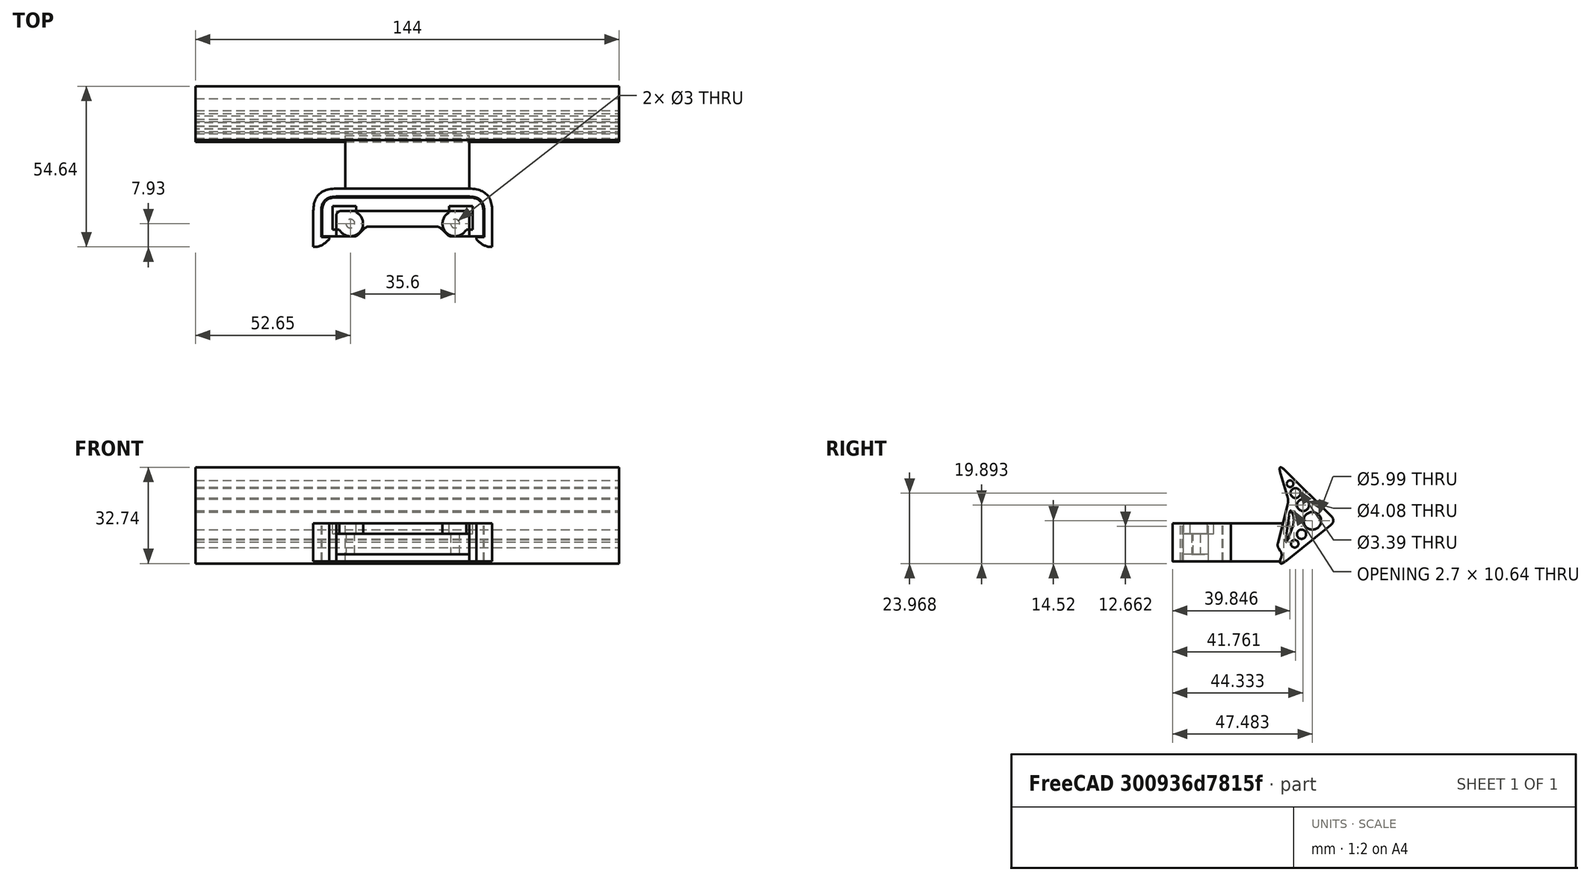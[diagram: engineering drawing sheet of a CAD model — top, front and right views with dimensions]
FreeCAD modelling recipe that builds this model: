
FCSTD DOCUMENT  (FreeCAD 0.19R0.19.2)
Label: 026
License: All rights reserved
LicenseURL: http://en.wikipedia.org/wiki/All_rights_reserved
objects: Sketcher::SketchObject×5, Part::Extrusion×5, Part::Box×1
note: 11 computed .brp shape members not serialized (recipe doc carries the construction recipe); baked Part::Feature solids carry a one-line shape summary decoded from their .brp

FEATURE [Sketcher::SketchObject] Sketch  label="attatchmentPiece"
  FullyConstrained = true
  sketch-geometry (20):
    g0: Circle CenterX=16.25 CenterY=0 CenterZ=0 NormalX=0 NormalY=0 NormalZ=1 AngleXU=0 Radius=1.5
    g1: LineSegment StartX=21.05 StartY=0 StartZ=0 EndX=21.05 EndY=-1 EndZ=0
    g2: LineSegment StartX=21.05 StartY=-1 StartZ=0 EndX=21.05 EndY=-4.3 EndZ=0
    g3: LineSegment StartX=-24.15 StartY=4.3 StartZ=0 EndX=21.05 EndY=4.3 EndZ=0
    g4: LineSegment StartX=21.05 StartY=0 StartZ=0 EndX=21.05 EndY=4.3 EndZ=0
    g5-g8: Circle x4 (B-spline internal-alignment scaffolding for g9; pole/knot coordinates omitted)
    g9: BSplineCurve PolesCount=4 KnotsCount=2 Degree=3 IsPeriodic=0
    g10: GeomPoint X=10.05 Y=-1 Z=0
    g11: GeomPoint X=14.55 Y=-4.3 Z=0
    g12: LineSegment StartX=10.05 StartY=-1 StartZ=0 EndX=-10.05 EndY=-1 EndZ=0
    g13: LineSegment StartX=14.55 StartY=-4.3 StartZ=0 EndX=21.05 EndY=-4.3 EndZ=0
    g14: LineSegment StartX=-24.15 StartY=4.3 StartZ=0 EndX=-24.15 EndY=-4.3 EndZ=0
    g15: LineSegment StartX=-13.15 StartY=-1 StartZ=0 EndX=-10.05 EndY=-1 EndZ=0
    g16: LineSegment StartX=-24.15 StartY=-4.3 StartZ=0 EndX=-19.35 EndY=-4.3 EndZ=0
    g17: Circle CenterX=-19.35 CenterY=0 CenterZ=0 NormalX=0 NormalY=0 NormalZ=1 AngleXU=0 Radius=1.5
    g18: LineSegment StartX=-19.35 StartY=-4.3 StartZ=0 EndX=-17.65 EndY=-4.3 EndZ=0
    g19: BSplineCurve PolesCount=4 KnotsCount=2 Degree=3 IsPeriodic=0
  constraints (41):
    c: Block(g0)
    c: Vertical(g1)
    c: Coincident(g2,g1)
    c: Vertical(g2)
    c: Block(g1)
    c: Horizontal(g3)
    c: Vertical(g4)
    c: Coincident(g4,g3)
    c: Block(g3)
    c: Block(g4)
    c: Weight(g5) = 1
    c: Equal(g5,g6)
    c: Equal(g5,g7)
    c: Equal(g5,g8)
    c: InternalAlignment(g5-g8 -> g9) x4
    c: InternalAlignment(g10,g9)
    c: InternalAlignment(g11,g9)
    c: Block(g9)
    c: Coincident(g12,g9)
    c: Horizontal(g12)
    c: Coincident(g13,g9)
    c: Coincident(g13,g2)
    c: Horizontal(g13)
    c: Distance(g3) = 45.2
    c: Coincident(g14,g3)
    c: Vertical(g14)
    c: Horizontal(g15)
    c: Distance(g15) = 3.1
    c: Block(g17)
    c: Horizontal(g16)
    c: Block(g19)
    c: Coincident(g18,g16)
    c: Coincident(g18,g19)
    c: Horizontal(g18)
    c: Block(g18)
    c: Coincident(g19,g15)
    c: Block(g16)
    c: Block(g12)
    c: Block(g14)
    c: Distance(g16) = 4.8
    c: Distance(g18) = 1.7
FEATURE [Part::Extrusion] Extrude  label="attatchmentPiece001"
  Base = -> Sketch
  Dir = (0,0,1)
  DirMode = 2
  FaceMakerClass = Part::FaceMakerBullseye
  LengthFwd = 7
  LengthRev = 0
  Solid = true
  Symmetric = false
FEATURE [Sketcher::SketchObject] Sketch001  label="attatchmentPieceSurround"
  FullyConstrained = true
  sketch-geometry (19):
    g0: LineSegment StartX=25.85 StartY=-4.3 StartZ=0 EndX=21.05 EndY=-4.3 EndZ=0
    g1: LineSegment StartX=25.85 StartY=-4.3 StartZ=0 EndX=25.85 EndY=4.3 EndZ=0
    g2: LineSegment StartX=-21.05 StartY=8.9 StartZ=0 EndX=21.05 EndY=8.9 EndZ=0
    g3: Circle CenterX=21.05 CenterY=8.9 CenterZ=0 NormalX=0 NormalY=0 NormalZ=1 AngleXU=0 Radius=1
    g4: Circle CenterX=25.85 CenterY=8.9 CenterZ=0 NormalX=0 NormalY=0 NormalZ=1 AngleXU=0 Radius=1
    g5: Circle CenterX=25.85 CenterY=4.3 CenterZ=0 NormalX=0 NormalY=0 NormalZ=1 AngleXU=0 Radius=1
    g6: BSplineCurve PolesCount=3 KnotsCount=2 Degree=2 IsPeriodic=0
    g7: GeomPoint X=21.05 Y=8.9 Z=0
    g8: GeomPoint X=25.85 Y=4.3 Z=0
    g9: ArcOfCircle CenterX=19.45 CenterY=2.7 CenterZ=0 NormalX=0 NormalY=0 NormalZ=1 AngleXU=0 Radius=1.6 StartAngle=0 EndAngle=1.5708
    g10: LineSegment StartX=-19.45 StartY=4.3 StartZ=0 EndX=19.45 EndY=4.3 EndZ=0
    g11: LineSegment StartX=21.05 StartY=2.7 StartZ=0 EndX=21.05 EndY=-4.3 EndZ=0
    g12: BSplineCurve PolesCount=3 KnotsCount=2 Degree=2 IsPeriodic=0
    g13: LineSegment StartX=-28.95 StartY=-4.3 StartZ=0 EndX=-28.95 EndY=4.3 EndZ=0
    g14: LineSegment StartX=-24.15 StartY=-4.3 StartZ=0 EndX=-28.95 EndY=-4.3 EndZ=0
    g15: LineSegment StartX=-24.15 StartY=2.7 StartZ=0 EndX=-24.15 EndY=-4.3 EndZ=0
    g16: ArcOfCircle CenterX=-22.55 CenterY=2.7 CenterZ=0 NormalX=0 NormalY=0 NormalZ=1 AngleXU=0 Radius=1.6 StartAngle=1.5708 EndAngle=3.14159
    g17: LineSegment StartX=-22.55 StartY=4.3 StartZ=0 EndX=-19.45 EndY=4.3 EndZ=0
    g18: LineSegment StartX=-24.15 StartY=8.9 StartZ=0 EndX=-21.05 EndY=8.9 EndZ=0
  constraints (41):
    c: Horizontal(g0)
    c: Vertical(g1)
    c: Coincident(g1,g0)
    c: Horizontal(g2)
    c: Distance(g2) = 42.1
    c: Block(g2)
    c: Coincident(g6,g2)
    c: Weight(g3) = 1
    c: Equal(g3,g4)
    c: Equal(g3,g5)
    c: Coincident(g6,g1)
    c: InternalAlignment(g3,g6)
    c: InternalAlignment(g4,g6)
    c: InternalAlignment(g5,g6)
    c: InternalAlignment(g7,g6)
    c: InternalAlignment(g8,g6)
    c: Block(g0)
    c: Block(g6)
    c: Block(g9)
    c: Coincident(g10,g9)
    c: Horizontal(g10)
    c: Coincident(g11,g9)
    c: Coincident(g11,g0)
    c: Vertical(g11)
    c: Horizontal(g14)
    c: Coincident(g13,g14)
    c: Vertical(g13)
    c: Coincident(g12,g13)
    c: Block(g13)
    c: Block(g12)
    c: Block(g16)
    c: Coincident(g15,g16)
    c: Coincident(g15,g14)
    c: Vertical(g15)
    c: Block(g10)
    c: Coincident(g17,g16)
    c: Coincident(g17,g10)
    c: Horizontal(g17)
    c: Coincident(g18,g12)
    c: Coincident(g18,g2)
    c: Horizontal(g18)
FEATURE [Part::Extrusion] Extrude001  label="attatchmentPieceSurround001"
  Base = -> Sketch001
  Dir = (0,0,1)
  DirMode = 2
  FaceMakerClass = Part::FaceMakerBullseye
  LengthFwd = 13
  LengthRev = 0
  Placement = pos=(0,0,-2.4) rot=(0,0,1;0rad)
  Solid = true
  Symmetric = false
FEATURE [Sketcher::SketchObject] Sketch002  label="attatchmentPieceEndScrewHoleCaps"
  FullyConstrained = true
  sketch-geometry (10):
    g0: ArcOfCircle CenterX=16.25 CenterY=0 CenterZ=0 NormalX=0 NormalY=0 NormalZ=1 AngleXU=0 Radius=4.3 StartAngle=2.05456 EndAngle=5.79942
    g1: LineSegment StartX=14.25 StartY=3.80657 StartZ=0 EndX=14.25 EndY=6 EndZ=0
    g2: LineSegment StartX=20.0566 StartY=-2 StartZ=0 EndX=22.25 EndY=-2 EndZ=0
    g3: LineSegment StartX=22.25 StartY=-2 StartZ=0 EndX=22.25 EndY=6 EndZ=0
    g4: LineSegment StartX=14.25 StartY=6 StartZ=0 EndX=22.25 EndY=6 EndZ=0
    g5: LineSegment StartX=-25.35 StartY=-2 StartZ=0 EndX=-25.35 EndY=6 EndZ=0
    g6: LineSegment StartX=-25.35 StartY=-2 StartZ=0 EndX=-23.1566 EndY=-2 EndZ=0
    g7: LineSegment StartX=-17.35 StartY=6 StartZ=0 EndX=-25.35 EndY=6 EndZ=0
    g8: LineSegment StartX=-17.35 StartY=3.80657 StartZ=0 EndX=-17.35 EndY=6 EndZ=0
    g9: ArcOfCircle CenterX=-19.35 CenterY=0 CenterZ=0 NormalX=0 NormalY=0 NormalZ=1 AngleXU=0 Radius=4.3 StartAngle=3.62536 EndAngle=7.37022
  constraints (25):
    c: Block(g0)
    c: Vertical(g1)
    c: Horizontal(g2)
    c: Coincident(g3,g2)
    c: Vertical(g3)
    c: Coincident(g4,g1)
    c: Horizontal(g4)
    c: Coincident(g3,g4)
    c: Block(g4)
    c: Block(g3)
    c: Coincident(g0,g1)
    c: Coincident(g0,g2)
    c: Block(g1)
    c: Block(g9)
    c: Horizontal(g6)
    c: Vertical(g8)
    c: Coincident(g7,g8)
    c: Horizontal(g7)
    c: Coincident(g5,g6)
    c: Vertical(g5)
    c: Coincident(g5,g7)
    c: Block(g7)
    c: Block(g5)
    c: Coincident(g9,g6)
    c: Coincident(g9,g8)
FEATURE [Part::Extrusion] Extrude002  label="attatchmentPieceEndScrewHoleCaps001"
  Base = -> Sketch002
  Dir = (0,0,1)
  DirMode = 2
  FaceMakerClass = Part::FaceMakerBullseye
  LengthFwd = 3.6
  LengthRev = 0
  Placement = pos=(0,0,7) rot=(0,0,1;0rad)
  Solid = true
  Symmetric = false
FEATURE [Sketcher::SketchObject] Sketch003  label="mainBumpperPieceAttatchment"
  FullyConstrained = true
  sketch-geometry (42):
    g0: Circle CenterX=28.85 CenterY=4.3 CenterZ=0 NormalX=0 NormalY=0 NormalZ=1 AngleXU=0 Radius=1
    g1: Circle CenterX=28.85 CenterY=11.9 CenterZ=0 NormalX=0 NormalY=0 NormalZ=1 AngleXU=0 Radius=1
    g2: Circle CenterX=21.05 CenterY=11.9 CenterZ=0 NormalX=0 NormalY=0 NormalZ=1 AngleXU=0 Radius=1
    g3: BSplineCurve PolesCount=3 KnotsCount=2 Degree=2 IsPeriodic=0
    g4: GeomPoint X=28.85 Y=4.3 Z=0
    g5: GeomPoint X=21.05 Y=11.9 Z=0
    g6: LineSegment StartX=-21.05 StartY=11.9 StartZ=0 EndX=21.05 EndY=11.9 EndZ=0
    g7: LineSegment StartX=28.85 StartY=4.3 StartZ=0 EndX=28.85 EndY=-4.3 EndZ=0
    g8: Circle CenterX=21.05 CenterY=9.2 CenterZ=0 NormalX=0 NormalY=0 NormalZ=1 AngleXU=0 Radius=1
    g9: Circle CenterX=26.15 CenterY=9.2 CenterZ=0 NormalX=0 NormalY=0 NormalZ=1 AngleXU=0 Radius=1
    g10: Circle CenterX=26.15 CenterY=4.3 CenterZ=0 NormalX=0 NormalY=0 NormalZ=1 AngleXU=0 Radius=1
    g11: BSplineCurve PolesCount=3 KnotsCount=2 Degree=2 IsPeriodic=0
    g12: GeomPoint X=21.05 Y=9.2 Z=0
    g13: GeomPoint X=26.15 Y=4.3 Z=0
    g14: LineSegment StartX=-21.05 StartY=9.2 StartZ=0 EndX=21.05 EndY=9.2 EndZ=0
    g15: LineSegment StartX=26.15 StartY=-4.3 StartZ=0 EndX=26.15 EndY=4.3 EndZ=0
    g16: LineSegment StartX=26.15 StartY=-4.3 StartZ=0 EndX=26.15 EndY=-4.6 EndZ=0
    g17: LineSegment StartX=23.45 StartY=-4.6 StartZ=0 EndX=26.15 EndY=-4.6 EndZ=0
    g18: LineSegment StartX=28.85 StartY=-4.3 StartZ=0 EndX=28.85 EndY=-7.9 EndZ=0
    g19: LineSegment StartX=23.45 StartY=-4.6 StartZ=0 EndX=23.45 EndY=-5.3 EndZ=0
    g20: Circle CenterX=28.85 CenterY=-7.9 CenterZ=0 NormalX=0 NormalY=0 NormalZ=1 AngleXU=0 Radius=1
    g21: Circle CenterX=26.15 CenterY=-8.2 CenterZ=0 NormalX=0 NormalY=0 NormalZ=1 AngleXU=0 Radius=1
    g22: Circle CenterX=23.45 CenterY=-5.3 CenterZ=0 NormalX=0 NormalY=0 NormalZ=1 AngleXU=0 Radius=1
    g23: BSplineCurve PolesCount=3 KnotsCount=2 Degree=2 IsPeriodic=0
    g24: GeomPoint X=28.85 Y=-7.9 Z=0
    g25: GeomPoint X=23.45 Y=-5.3 Z=0
    g26: LineSegment StartX=-21.05 StartY=9.2 StartZ=0 EndX=-24.15 EndY=9.2 EndZ=0
    g27: BSplineCurve PolesCount=3 KnotsCount=2 Degree=2 IsPeriodic=0
    g28: LineSegment StartX=-29.25 StartY=-4.3 StartZ=0 EndX=-29.25 EndY=-4.6 EndZ=0
    g29: LineSegment StartX=-29.25 StartY=-4.6 StartZ=0 EndX=-26.55 EndY=-4.6 EndZ=0
    g30: LineSegment StartX=-31.95 StartY=-4.3 StartZ=0 EndX=-31.95 EndY=-7.9 EndZ=0
    g31: LineSegment StartX=-26.55 StartY=-4.6 StartZ=0 EndX=-26.55 EndY=-5.3 EndZ=0
    g32: Circle CenterX=-31.95 CenterY=-7.9 CenterZ=0 NormalX=0 NormalY=0 NormalZ=1 AngleXU=0 Radius=1
    g33: Circle CenterX=-29.25 CenterY=-8.2 CenterZ=0 NormalX=0 NormalY=0 NormalZ=1 AngleXU=0 Radius=1
    g34: Circle CenterX=-26.55 CenterY=-5.3 CenterZ=0 NormalX=0 NormalY=0 NormalZ=1 AngleXU=0 Radius=1
    g35: BSplineCurve PolesCount=3 KnotsCount=2 Degree=2 IsPeriodic=0
    g36: GeomPoint X=-31.95 Y=-7.9 Z=0
    g37: GeomPoint X=-26.55 Y=-5.3 Z=0
    g38: LineSegment StartX=-31.95 StartY=4.3 StartZ=0 EndX=-31.95 EndY=-4.3 EndZ=0
    g39: LineSegment StartX=-29.25 StartY=-4.3 StartZ=0 EndX=-29.25 EndY=4.3 EndZ=0
    g40: BSplineCurve PolesCount=3 KnotsCount=2 Degree=2 IsPeriodic=0
    g41: LineSegment StartX=-21.05 StartY=11.9 StartZ=0 EndX=-24.15 EndY=11.9 EndZ=0
  constraints (78):
    c: Weight(g0) = 1
    c: Equal(g0,g1)
    c: Equal(g0,g2)
    c: InternalAlignment(g0,g3)
    c: InternalAlignment(g1,g3)
    c: InternalAlignment(g2,g3)
    c: InternalAlignment(g4,g3)
    c: InternalAlignment(g5,g3)
    c: Block(g3)
    c: Horizontal(g6)
    c: Vertical(g7)
    c: Block(g7)
    c: Block(g6)
    c: Weight(g8) = 1
    c: Equal(g8,g9)
    c: Equal(g8,g10)
    c: InternalAlignment(g8,g11)
    c: InternalAlignment(g9,g11)
    c: InternalAlignment(g10,g11)
    c: InternalAlignment(g12,g11)
    c: InternalAlignment(g13,g11)
    c: Horizontal(g14)
    c: Vertical(g15)
    c: Block(g11)
    c: Block(g15)
    c: Block(g14)
    c: Coincident(g16,g15)
    c: Vertical(g16)
    c: Distance(g16) = 0.3
    c: Horizontal(g17)
    c: Coincident(g17,g16)
    c: Coincident(g18,g7)
    c: Vertical(g18)
    c: Distance(g18) = 3.6
    c: Vertical(g19)
    c: Coincident(g19,g17)
    c: Coincident(g23,g18)
    c: Weight(g20) = 1
    c: Equal(g20,g21)
    c: Equal(g20,g22)
    c: Coincident(g23,g19)
    c: InternalAlignment(g20,g23)
    c: InternalAlignment(g21,g23)
    c: InternalAlignment(g22,g23)
    c: InternalAlignment(g24,g23)
    c: InternalAlignment(g25,g23)
    c: Block(g23)
    c: Horizontal(g26)
    c: Distance(g26) = 3.1
    c: Block(g27)
    c: Vertical(g38)
    c: Block(g38)
    c: Vertical(g39)
    c: Block(g40)
    c: Block(g39)
    c: Vertical(g28)
    c: Coincident(g28,g39)
    c: Coincident(g29,g28)
    c: Horizontal(g29)
    c: Vertical(g30)
    c: Coincident(g30,g38)
    c: Coincident(g31,g29)
    c: Vertical(g31)
    c: Coincident(g35,g30)
    c: Equal(g32,g33)
    c: Equal(g32,g34)
    c: Coincident(g35,g31)
    c: InternalAlignment(g32,g35)
    c: InternalAlignment(g33,g35)
    c: InternalAlignment(g34,g35)
    c: InternalAlignment(g36,g35)
    c: InternalAlignment(g37,g35)
    c: Block(g35)
    c: Coincident(g40,g26)
    c: Block(g29)
    c: Horizontal(g41)
    c: Equal(g26,g41) = 3.1
    c: Coincident(g41,g6)
FEATURE [Part::Extrusion] Extrude003  label="mainBumpperPieceAttatchment001"
  Base = -> Sketch003
  Dir = (0,0,1)
  DirMode = 2
  FaceMakerClass = Part::FaceMakerBullseye
  LengthFwd = 13
  LengthRev = 0
  Placement = pos=(0,0,-2.4) rot=(0,0,1;0rad)
  Solid = true
  Symmetric = false
FEATURE [Part::Box] Box  label="bumpperExtension"
  AttacherType = Attacher::AttachEngine3D
  Height = 13
  Length = 42.1
  Placement = pos=(-21.05,11.9,-2.4) rot=(0,0,1;0rad)
  Width = 18
FEATURE [Sketcher::SketchObject] Sketch004  label="bumpperMain"
  FullyConstrained = true
  Placement = pos=(0,0,0) rot=(0.57735,0.57735,0.57735;2.0944rad)
  sketch-geometry (62):
    g0: Circle CenterX=-3.12329 CenterY=2.49901 CenterZ=0 NormalX=0 NormalY=0 NormalZ=1 AngleXU=0 Radius=1
    g1: Circle CenterX=0 CenterY=0 CenterZ=0 NormalX=0 NormalY=0 NormalZ=1 AngleXU=0 Radius=1
    g2: Circle CenterX=-1.35243 CenterY=3.60648 CenterZ=0 NormalX=0 NormalY=0 NormalZ=1 AngleXU=0 Radius=1
    g3: BSplineCurve PolesCount=3 KnotsCount=2 Degree=2 IsPeriodic=0
    g4: GeomPoint X=-3.12329 Y=2.49901 Z=0
    g5: GeomPoint X=-1.35243 Y=3.60648 Z=0
    g6: Circle CenterX=-2.83953 CenterY=33.0261 CenterZ=0 NormalX=0 NormalY=0 NormalZ=1 AngleXU=0 Radius=1
    g7: Circle CenterX=0 CenterY=35.8434 CenterZ=0 NormalX=0 NormalY=0 NormalZ=1 AngleXU=0 Radius=1
    g8: Circle CenterX=-1.15771 CenterY=32.0146 CenterZ=0 NormalX=0 NormalY=0 NormalZ=1 AngleXU=0 Radius=1
    g9: BSplineCurve PolesCount=3 KnotsCount=2 Degree=2 IsPeriodic=0
    g10: GeomPoint X=-2.83953 Y=33.0261 Z=0
    g11: GeomPoint X=-1.15771 Y=32.0146 Z=0
    g12: Circle CenterX=-18.2963 CenterY=17.6904 CenterZ=0 NormalX=0 NormalY=0 NormalZ=1 AngleXU=0 Radius=1
    g13: Circle CenterX=-20 CenterY=16 CenterZ=0 NormalX=0 NormalY=0 NormalZ=1 AngleXU=0 Radius=1
    g14: Circle CenterX=-18.1259 CenterY=14.5008 CenterZ=0 NormalX=0 NormalY=0 NormalZ=1 AngleXU=0 Radius=1
    g15: BSplineCurve PolesCount=3 KnotsCount=2 Degree=2 IsPeriodic=0
    g16: GeomPoint X=-18.2963 Y=17.6904 Z=0
    g17: GeomPoint X=-18.1259 Y=14.5008 Z=0
    g18: LineSegment StartX=-18.2963 StartY=17.6904 StartZ=0 EndX=-2.83953 EndY=33.0261 EndZ=0
    g19: LineSegment StartX=-18.1259 StartY=14.5008 StartZ=0 EndX=-3.12329 EndY=2.49901 EndZ=0
    g20: Circle CenterX=-11.9527 CenterY=16 CenterZ=0 NormalX=0 NormalY=0 NormalZ=1 AngleXU=0 Radius=2.99582
    g21: Circle CenterX=-8.803 CenterY=21.3731 CenterZ=0 NormalX=0 NormalY=0 NormalZ=1 AngleXU=0 Radius=2.03939
    g22: Circle CenterX=-6.23123 CenterY=25.4475 CenterZ=0 NormalX=0 NormalY=0 NormalZ=1 AngleXU=0 Radius=1.69309
    g23: Circle CenterX=-4.38186 CenterY=28.6261 CenterZ=0 NormalX=0 NormalY=0 NormalZ=1 AngleXU=0 Radius=1.13029
    g24: Circle CenterX=-8.28033 CenterY=11.4296 CenterZ=0 NormalX=0 NormalY=0 NormalZ=1 AngleXU=0 Radius=1.57213
    g25: Circle CenterX=-5.93972 CenterY=8.22213 CenterZ=0 NormalX=0 NormalY=0 NormalZ=1 AngleXU=0 Radius=1.28743
    g26: Circle CenterX=-3.47023 CenterY=24.3665 CenterZ=0 NormalX=0 NormalY=0 NormalZ=1 AngleXU=0 Radius=1
    g27: Circle CenterX=-3.90437 CenterY=22.9307 CenterZ=0 NormalX=0 NormalY=0 NormalZ=1 AngleXU=0 Radius=1
    g28: Circle CenterX=-3.53772 CenterY=21.4762 CenterZ=0 NormalX=0 NormalY=0 NormalZ=1 AngleXU=0 Radius=1
    g29: BSplineCurve PolesCount=3 KnotsCount=2 Degree=2 IsPeriodic=0
    g30: GeomPoint X=-3.47023 Y=24.3665 Z=0
    g31: GeomPoint X=-3.53772 Y=21.4762 Z=0
    g32: LineSegment StartX=-1.15771 StartY=32.0146 StartZ=0 EndX=-3.47023 EndY=24.3665 EndZ=0
    g33: Circle CenterX=-5.41867 CenterY=17.9226 CenterZ=0 NormalX=0 NormalY=0 NormalZ=1 AngleXU=0 Radius=1
    g34: Circle CenterX=-6 CenterY=16 CenterZ=0 NormalX=0 NormalY=0 NormalZ=1 AngleXU=0 Radius=1
    g35: Circle CenterX=-5.22753 CenterY=13.9401 CenterZ=0 NormalX=0 NormalY=0 NormalZ=1 AngleXU=0 Radius=1
    g36: BSplineCurve PolesCount=3 KnotsCount=2 Degree=2 IsPeriodic=0
    g37: GeomPoint X=-5.41867 Y=17.9226 Z=0
    g38: GeomPoint X=-5.22753 Y=13.9401 Z=0
    g39: Circle CenterX=-3.98946 CenterY=10.6386 CenterZ=0 NormalX=0 NormalY=0 NormalZ=1 AngleXU=0 Radius=1
    g40: Circle CenterX=-2.58497 CenterY=6.89324 CenterZ=0 NormalX=0 NormalY=0 NormalZ=1 AngleXU=0 Radius=1
    g41: Circle CenterX=-3.11001 CenterY=10.8586 CenterZ=0 NormalX=0 NormalY=0 NormalZ=1 AngleXU=0 Radius=1
    g42: BSplineCurve PolesCount=3 KnotsCount=2 Degree=2 IsPeriodic=0
    g43: GeomPoint X=-3.98946 Y=10.6386 Z=0
    g44: GeomPoint X=-3.11001 Y=10.8586 Z=0
    g45: Circle CenterX=-1.35243 CenterY=3.60648 CenterZ=0 NormalX=0 NormalY=0 NormalZ=1 AngleXU=0 Radius=1
    g46: Circle CenterX=-1.76142 CenterY=4.69712 CenterZ=0 NormalX=0 NormalY=0 NormalZ=1 AngleXU=0 Radius=1
    g47: Circle CenterX=-1.05937 CenterY=5.79125 CenterZ=0 NormalX=0 NormalY=0 NormalZ=1 AngleXU=0 Radius=1
    g48: BSplineCurve PolesCount=3 KnotsCount=2 Degree=2 IsPeriodic=0
    g49: GeomPoint X=-1.35243 Y=3.60648 Z=0
    g50: GeomPoint X=-1.05937 Y=5.79125 Z=0
    g51: Circle CenterX=-0.519336 CenterY=6.6329 CenterZ=0 NormalX=0 NormalY=0 NormalZ=1 AngleXU=0 Radius=1
    g52: Circle CenterX=0 CenterY=7.44228 CenterZ=0 NormalX=0 NormalY=0 NormalZ=1 AngleXU=0 Radius=1
    g53: Circle CenterX=-0.244436 CenterY=8.41194 CenterZ=0 NormalX=0 NormalY=0 NormalZ=1 AngleXU=0 Radius=1
    g54: BSplineCurve PolesCount=3 KnotsCount=2 Degree=2 IsPeriodic=0
    g55: GeomPoint X=-0.519336 Y=6.6329 Z=0
    g56: GeomPoint X=-0.244436 Y=8.41194 Z=0
    g57: LineSegment StartX=-3.53772 StartY=21.4762 StartZ=0 EndX=-0.244436 EndY=8.41194 EndZ=0
    g58: LineSegment StartX=-5.22753 StartY=13.9401 StartZ=0 EndX=-3.98946 EndY=10.6386 EndZ=0
    g59: LineSegment StartX=-1.05937 StartY=5.79125 StartZ=0 EndX=-0.519336 EndY=6.6329 EndZ=0
    g60: BSplineCurve PolesCount=3 KnotsCount=2 Degree=2 IsPeriodic=0
    g61: LineSegment StartX=-4.0304 StartY=17.8099 StartZ=0 EndX=-3.11001 EndY=10.8586 EndZ=0
  constraints (96):
    c: Weight(g0) = 1
    c: Equal(g0,g1)
    c: Equal(g0,g2)
    c: InternalAlignment(g0,g3)
    c: InternalAlignment(g1,g3)
    c: InternalAlignment(g2,g3)
    c: InternalAlignment(g4,g3)
    c: InternalAlignment(g5,g3)
    c: Block(g3)
    c: Weight(g6) = 1
    c: Equal(g6,g7)
    c: Equal(g6,g8)
    c: InternalAlignment(g6,g9)
    c: InternalAlignment(g7,g9)
    c: InternalAlignment(g8,g9)
    c: InternalAlignment(g10,g9)
    c: InternalAlignment(g11,g9)
    c: Block(g9)
    c: Weight(g12) = 1
    c: Equal(g12,g13)
    c: Equal(g12,g14)
    c: InternalAlignment(g12,g15)
    c: InternalAlignment(g13,g15)
    c: InternalAlignment(g14,g15)
    c: InternalAlignment(g16,g15)
    c: InternalAlignment(g17,g15)
    c: Block(g15)
    c: Coincident(g18,g15)
    c: Coincident(g18,g9)
    c: Coincident(g19,g15)
    c: Coincident(g19,g3)
    c: Block(g25)
    c: Block(g24)
    c: Block(g20)
    c: Block(g21)
    c: Block(g22)
    c: Block(g23)
    c: Weight(g26) = 1
    c: Equal(g26,g27)
    c: Equal(g26,g28)
    c: InternalAlignment(g26,g29)
    c: InternalAlignment(g27,g29)
    c: InternalAlignment(g28,g29)
    c: InternalAlignment(g30,g29)
    c: InternalAlignment(g31,g29)
    c: Block(g29)
    c: Coincident(g32,g9)
    c: Coincident(g32,g29)
    c: Weight(g33) = 1
    c: Equal(g33,g34)
    c: Equal(g33,g35)
    c: InternalAlignment(g33,g36)
    c: InternalAlignment(g34,g36)
    c: InternalAlignment(g35,g36)
    c: InternalAlignment(g37,g36)
    c: InternalAlignment(g38,g36)
    c: Block(g36)
    c: Weight(g39) = 1
    c: Equal(g39,g40)
    c: Equal(g39,g41)
    c: InternalAlignment(g39,g42)
    c: InternalAlignment(g40,g42)
    c: InternalAlignment(g41,g42)
    c: InternalAlignment(g43,g42)
    c: InternalAlignment(g44,g42)
    c: Block(g42)
    c: Coincident(g48,g3)
    c: Weight(g45) = 1
    c: Equal(g45,g46)
    c: Equal(g45,g47)
    c: InternalAlignment(g45,g48)
    c: InternalAlignment(g46,g48)
    c: InternalAlignment(g47,g48)
    c: InternalAlignment(g49,g48)
    c: InternalAlignment(g50,g48)
    c: Block(g48)
    c: Weight(g51) = 1
    c: Equal(g51,g52)
    c: Equal(g51,g53)
    c: InternalAlignment(g51,g54)
    c: InternalAlignment(g52,g54)
    c: InternalAlignment(g53,g54)
    c: InternalAlignment(g55,g54)
    c: InternalAlignment(g56,g54)
    c: Block(g54)
    c: Coincident(g57,g29)
    c: Coincident(g57,g54)
    c: Block(g57)
    c: Coincident(g58,g36)
    c: Coincident(g58,g42)
    c: Coincident(g59,g48)
    c: Coincident(g59,g54)
    c: Block(g60)
    c: Coincident(g60,g36)
    c: Coincident(g61,g60)
    c: Coincident(g61,g42)
FEATURE [Part::Extrusion] Extrude004  label="bumpperMain001"
  Base = -> Sketch004
  Dir = (1,0,0)
  DirMode = 2
  FaceMakerClass = Part::FaceMakerBullseye
  LengthFwd = 144
  LengthRev = 0
  Placement = pos=(72,27.6,-4.6) rot=(0,0,1;3.14159rad)
  Solid = true
  Symmetric = false
